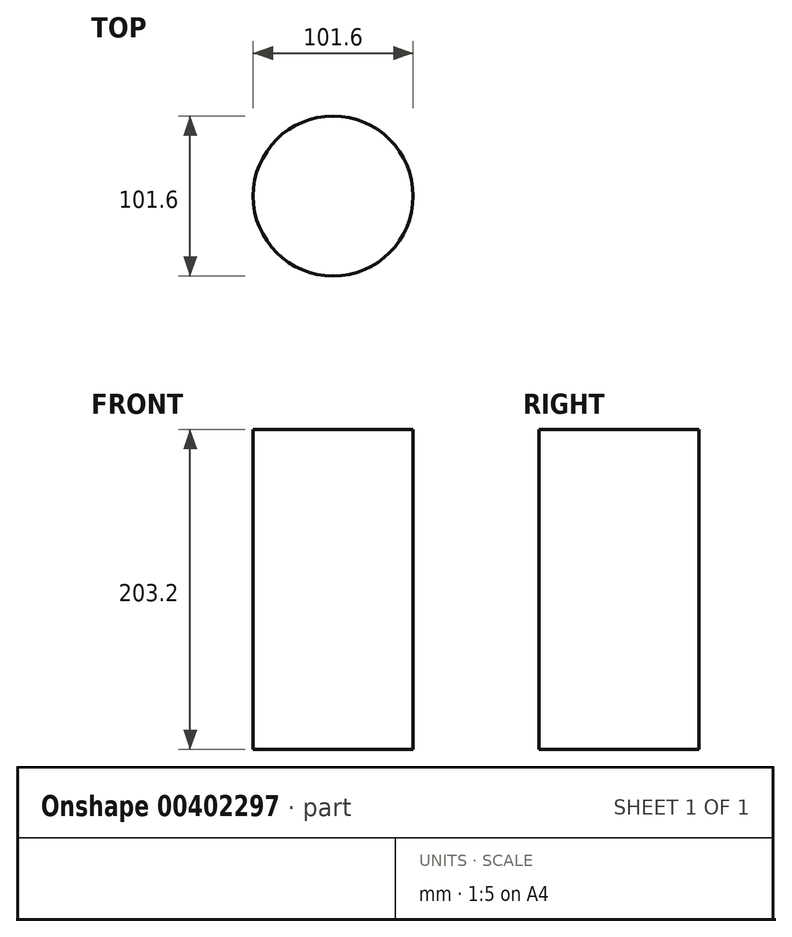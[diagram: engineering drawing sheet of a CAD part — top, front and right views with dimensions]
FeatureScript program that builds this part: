
annotation { "Feature Type Name" : "Feature", "Feature Type Description" : "" }
export const myFeature = defineFeature(function(context is Context, id is Id, definition is map)
    precondition{}
    {
        {
            var Q0;
            Q0=qCreatedBy(makeId("Top.planeOp"),FACE);
            var sketch = newSketch(context, id + "F0", { "sketchPlane" : qUnion([Q0])});
            skCircle(sketch, "E0", {"center": v(0, 0) * mm, "radius": 50.8 * mm});
            skSolve(sketch);
        }
        {
            var Q0;
            Q0 = qSketchRegion(id + "F0", true);
            extrude(context, id + "F1", {"entities" : qUnion([Q0]), "depth" : 203.2 * mm});
        }
    });
